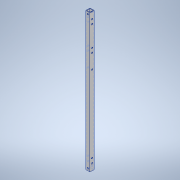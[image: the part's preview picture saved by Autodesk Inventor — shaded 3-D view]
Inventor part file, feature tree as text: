
AUTODESK INVENTOR PART (.ipt)
format: ipt  version: 2020.3 (Build 243373000, 373)  size: 164,864 bytes
history: native  units: mm
features: sketch x8, hole x7, other x1, extrude x1
ambient origin geometry x8: Origin, YZ Plane, XZ Plane, XY Plane, X Axis, Y Axis, Z Axis, Center Point
bodies: Body1 (feature_tree)
feature tree (17):
  other  "ソリッド1"
  extrude  "押し出し1"  Depth=9.0mm
  hole  "穴1"  [1 undecoded]
  hole  "穴2"  [1 undecoded]
  hole  "穴3"  [1 undecoded]
  hole  "穴4"  [1 undecoded]
  hole  "穴5"  [1 undecoded]
  hole  "穴6"  [1 undecoded]
  hole  "穴7"  [1 undecoded]
  sketch  "スケッチ1"
  sketch  "スケッチ2"
  sketch  "スケッチ3"
  sketch  "スケッチ4"
  sketch  "スケッチ5"
  sketch  "スケッチ6"
  sketch  "スケッチ7"
  sketch  "スケッチ8"
note: 7 required parameter values undecoded (feature->parameter linkage not recoverable at this tier; creation-order binding heuristic only, values carry confidence <= 0.55)
